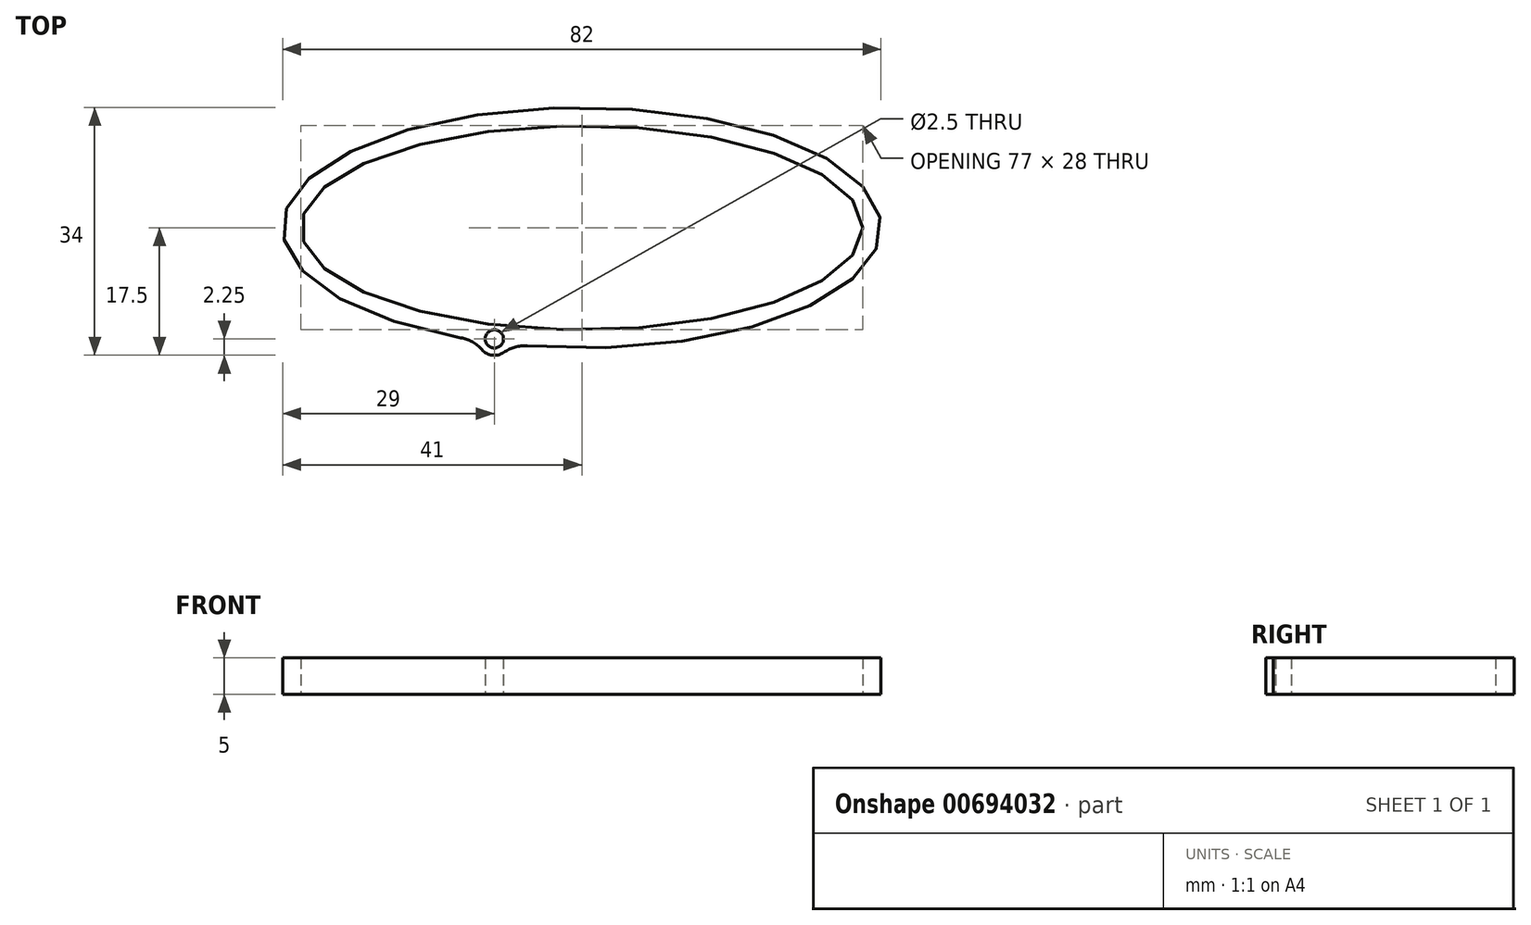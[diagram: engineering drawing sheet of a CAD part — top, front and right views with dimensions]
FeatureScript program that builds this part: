
annotation { "Feature Type Name" : "Feature", "Feature Type Description" : "" }
export const myFeature = defineFeature(function(context is Context, id is Id, definition is map)
    precondition{}
    {
        {
            var Q0;
            Q0=qCreatedBy(makeId("Top.planeOp"),FACE);
            var sketch = newSketch(context, id + "F0", { "sketchPlane" : qUnion([Q0])});
            skEllipse(sketch, "E0", {"center": v(0, 0) * mm, "majorRadius": 38.5 * mm, "minorRadius": 14 * mm, "majorAxis": v(1, 0)});
            skEllipticalArc(sketch, "E1", {});
            skLineSegment(sketch, "E2", {"start": v(0, 0) * mm, "end": v(0, -14) * mm});
            skLineSegment(sketch, "E3", {"start": v(0, -14) * mm, "end": v(0, -15.25) * mm});
            skCircle(sketch, "E4", {"center": v(-12, -15.25) * mm, "radius": 1.25 * mm});
            skArc(sketch, "E5", {"start": v(-13.7, -16.73) * mm, "mid": v(-12.28, -17.48) * mm, "end": v(-10.72, -17.1) * mm});
            skPoint(sketch, "E6.visualSharp", {"position": v(-14.24, -15.47) * mm});
            skArc(sketch, "E6.filletArc", {"start": v(-13.7, -16.73) * mm, "mid": v(-15, -15.66) * mm, "end": v(-16.6, -15.09) * mm});
            skPoint(sketch, "E7.visualSharp", {"position": v(-9.88, -16.01) * mm});
            skArc(sketch, "E7.filletArc", {"start": v(-7.5, -16.22) * mm, "mid": v(-9.18, -16.38) * mm, "end": v(-10.72, -17.1) * mm});
            const initialGuessF0  = {"E1": [0, 0, 1, 0, 0.041, 0.0165, 4.52852939372641, 4.295789254683701]};
            skSetInitialGuess(sketch, initialGuessF0);
            skSolve(sketch);
        }
        {
            var Q0;
            Q0=makeQuery(id+"F0.imprint","IMPRINT",FACE,{"disambiguationData":[TD([[makeQuery(id+"F0.imprint","IMPRINT",EDGE,{"derivedFrom":sQuery(id+"F0.wireOp",EDGE,"E0")}),-1.0]])]});
            extrude(context, id + "F1", {"entities" : qUnion([Q0]), "depth" : 5 * mm, "offsetDistance" : 25 * mm});
        }
    });
